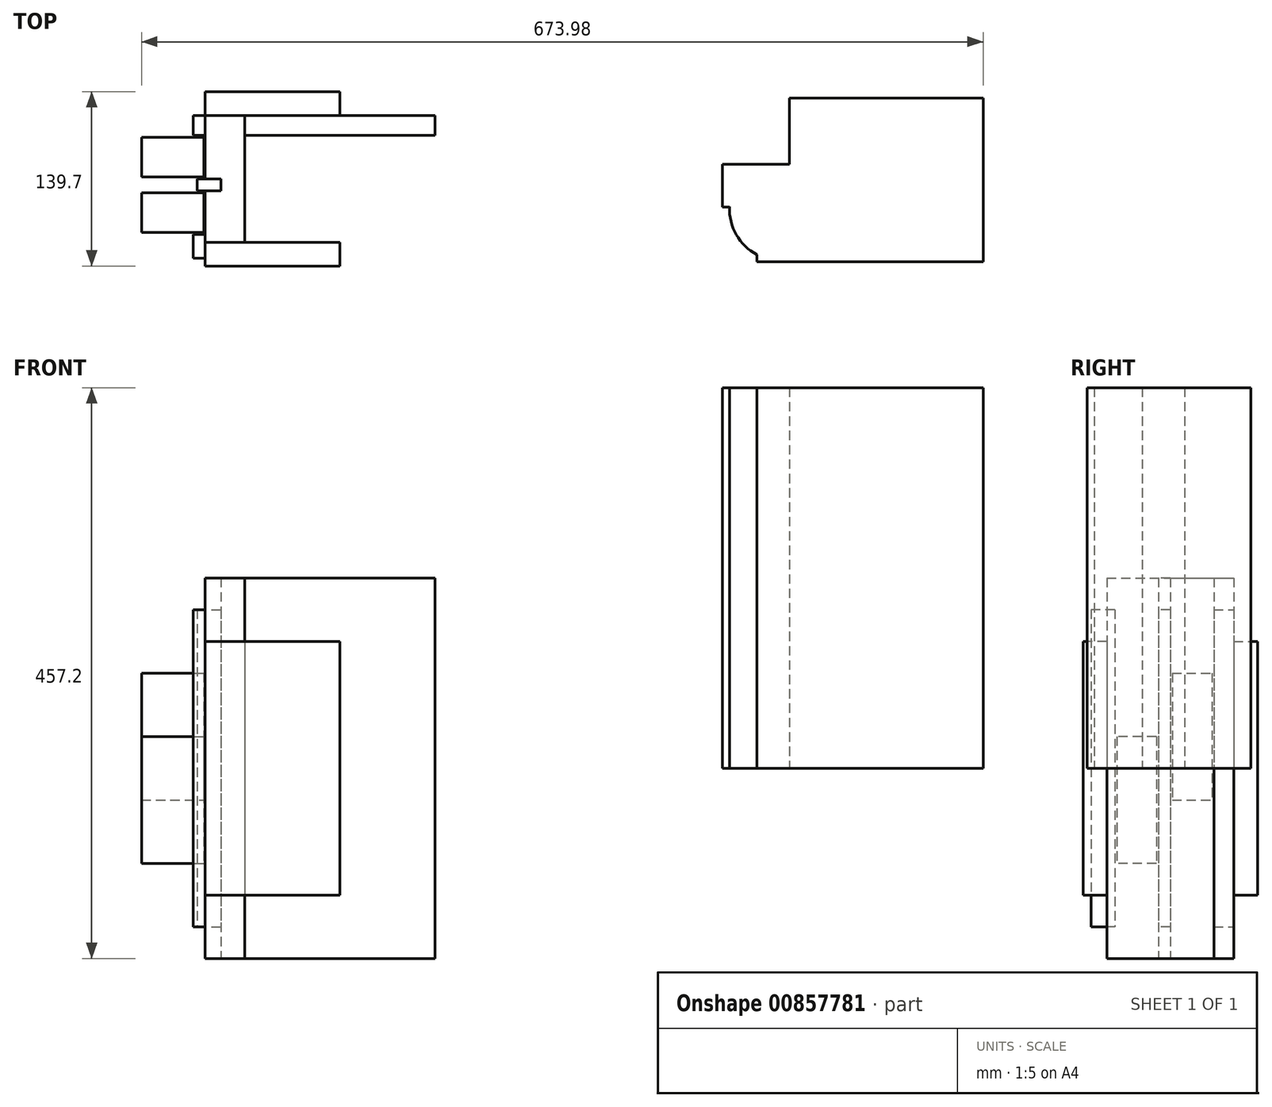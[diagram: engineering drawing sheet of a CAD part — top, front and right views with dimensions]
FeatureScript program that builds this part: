
annotation { "Feature Type Name" : "Feature", "Feature Type Description" : "" }
export const myFeature = defineFeature(function(context is Context, id is Id, definition is map)
    precondition{}
    {
        {
            var Q0;
            Q0=qCreatedBy(makeId("Top.planeOp"),FACE);
            var sketch = newSketch(context, id + "F0", { "sketchPlane" : qUnion([Q0])});
            skLineSegment(sketch, "E0.bottom", {"start": v(190.17, 63.13) * mm, "end": v(345.29, 63.13) * mm});
            skLineSegment(sketch, "E0.top", {"start": v(164.15, -68) * mm, "end": v(345.29, -68) * mm});
            skLineSegment(sketch, "E0.left", {"start": v(136.6, 10.06) * mm, "end": v(136.6, -24.12) * mm});
            skLineSegment(sketch, "E0.right", {"start": v(345.29, 63.13) * mm, "end": v(345.29, -68) * mm});
            skLineSegment(sketch, "E1.top", {"start": v(136.6, 10.06) * mm, "end": v(190.17, 10.06) * mm});
            skLineSegment(sketch, "E1.right", {"start": v(190.17, 63.13) * mm, "end": v(190.17, 10.06) * mm});
            skLineSegment(sketch, "E2.bottom", {"start": v(136.6, -24.12) * mm, "end": v(142.2, -24.12) * mm});
            skLineSegment(sketch, "E2.right", {"start": v(164.15, -62.4) * mm, "end": v(164.15, -68) * mm});
            skArc(sketch, "E3", {"start": v(142.2, -24.12) * mm, "mid": v(147.6, -46.46) * mm, "end": v(164.15, -62.4) * mm});
            skSolve(sketch);
        }
        {
            var Q0;
            Q0 = qSketchRegion(id + "F0", true);
            extrude(context, id + "F1", {"entities" : qUnion([Q0]), "depth" : 304.8 * mm, "offsetDistance" : 25.4 * mm});
        }
        {
            var Q0;
            Q0=qCreatedBy(makeId("Top.planeOp"),FACE);
            var sketch = newSketch(context, id + "F2", { "sketchPlane" : qUnion([Q0])});
            skLineSegment(sketch, "E4.bottom", {"start": v(-328.7, -12.7) * mm, "end": v(-278.69, -12.7) * mm});
            skLineSegment(sketch, "E4.top", {"start": v(-328.7, -44.45) * mm, "end": v(-278.69, -44.45) * mm});
            skLineSegment(sketch, "E4.left", {"start": v(-328.7, -12.7) * mm, "end": v(-328.7, -44.45) * mm});
            skLineSegment(sketch, "E4.right", {"start": v(-277.9, -12.7) * mm, "end": v(-277.9, -44.45) * mm});
            skLineSegment(sketch, "E5.bottom", {"start": v(-328.7, 0) * mm, "end": v(-278.69, 0) * mm});
            skLineSegment(sketch, "E5.top", {"start": v(-328.7, 31.75) * mm, "end": v(-278.69, 31.75) * mm});
            skLineSegment(sketch, "E5.left", {"start": v(-328.7, 0) * mm, "end": v(-328.7, 31.75) * mm});
            skLineSegment(sketch, "E5.right", {"start": v(-277.9, 0) * mm, "end": v(-277.9, 31.75) * mm});
            skLineSegment(sketch, "E6.bottom", {"start": v(-284.24, -1.59) * mm, "end": v(-265.2, -1.59) * mm});
            skLineSegment(sketch, "E6.top", {"start": v(-284.24, -11.11) * mm, "end": v(-265.2, -11.11) * mm});
            skLineSegment(sketch, "E6.left", {"start": v(-284.24, -1.59) * mm, "end": v(-284.24, -11.11) * mm});
            skLineSegment(sketch, "E6.right", {"start": v(-265.2, -1.59) * mm, "end": v(-265.2, -11.11) * mm});
            skLineSegment(sketch, "E7.bottom", {"start": v(-287.42, 33.34) * mm, "end": v(-277.9, 33.34) * mm});
            skLineSegment(sketch, "E7.top", {"start": v(-287.42, 49.21) * mm, "end": v(-277.9, 49.21) * mm});
            skLineSegment(sketch, "E7.left", {"start": v(-287.42, 33.34) * mm, "end": v(-287.42, 49.21) * mm});
            skLineSegment(sketch, "E7.right", {"start": v(-277.9, 33.34) * mm, "end": v(-277.9, 49.21) * mm});
            skLineSegment(sketch, "E8.bottom", {"start": v(-287.42, -46.04) * mm, "end": v(-277.9, -46.04) * mm});
            skLineSegment(sketch, "E8.top", {"start": v(-287.42, -65.09) * mm, "end": v(-277.9, -65.09) * mm});
            skLineSegment(sketch, "E8.left", {"start": v(-287.42, -46.04) * mm, "end": v(-287.42, -65.09) * mm});
            skLineSegment(sketch, "E8.right", {"start": v(-277.9, -46.04) * mm, "end": v(-277.9, -65.09) * mm});
            skLineSegment(sketch, "E9.top", {"start": v(-277.9, 49.21) * mm, "end": v(-246.14, 49.21) * mm});
            skLineSegment(sketch, "E9.left", {"start": v(-277.9, -71.44) * mm, "end": v(-277.9, -11.11) * mm});
            skLineSegment(sketch, "E9.right", {"start": v(-246.14, -52.39) * mm, "end": v(-246.14, 49.21) * mm});
            skLineSegment(sketch, "E10.bottom", {"start": v(-277.9, 49.21) * mm, "end": v(-169.94, 49.21) * mm});
            skLineSegment(sketch, "E10.top", {"start": v(-277.9, 68.26) * mm, "end": v(-169.94, 68.26) * mm});
            skLineSegment(sketch, "E10.left", {"start": v(-277.9, 49.21) * mm, "end": v(-277.9, 68.26) * mm});
            skLineSegment(sketch, "E10.right", {"start": v(-169.94, 49.21) * mm, "end": v(-169.94, 68.26) * mm});
            skLineSegment(sketch, "E11.bottom", {"start": v(-277.9, -52.39) * mm, "end": v(-169.94, -52.39) * mm});
            skLineSegment(sketch, "E11.top", {"start": v(-277.9, -71.44) * mm, "end": v(-169.94, -71.44) * mm});
            skLineSegment(sketch, "E11.left", {"start": v(-277.9, -52.39) * mm, "end": v(-277.9, -71.44) * mm});
            skLineSegment(sketch, "E11.right", {"start": v(-169.94, -52.39) * mm, "end": v(-169.94, -71.44) * mm});
            skLineSegment(sketch, "E12.trimOffspring", {"start": v(-277.9, -1.59) * mm, "end": v(-277.9, 49.21) * mm});
            skLineSegment(sketch, "E13", {"start": v(-278.69, 31.75) * mm, "end": v(-278.69, 0) * mm});
            skLineSegment(sketch, "E14", {"start": v(-278.69, -12.7) * mm, "end": v(-278.69, -44.45) * mm});
            skLineSegment(sketch, "E15.bottom", {"start": v(-246.14, 49.21) * mm, "end": v(-93.74, 49.21) * mm});
            skLineSegment(sketch, "E15.top", {"start": v(-246.14, 33.34) * mm, "end": v(-93.74, 33.34) * mm});
            skLineSegment(sketch, "E15.left", {"start": v(-246.14, 49.21) * mm, "end": v(-246.14, 33.34) * mm});
            skLineSegment(sketch, "E15.right", {"start": v(-93.74, 49.21) * mm, "end": v(-93.74, 33.34) * mm});
            skSolve(sketch);
        }
        {
            var Q0;
            Q0=makeQuery(id+"F2.imprint","IMPRINT",FACE,{"disambiguationData":[TD([[makeQuery(id+"F2.imprint","IMPRINT",EDGE,{"derivedFrom":sQuery(id+"F2.wireOp",EDGE,"E5.bottom")}),1.0]])]});
            extrude(context, id + "F3", {"entities" : qUnion([Q0]), "depth" : 76.2 * mm, "offsetDistance" : 25.4 * mm, "hasSecondDirection" : true, "secondDirectionOppositeDirection" : true, "secondDirectionDepth" : 25.4 * mm});
        }
        {
            var Q0;
            {var subQ0=sQuery(id+"F2.wireOp",EDGE,"E7.bottom");Q0=makeQuery(id+"F2.imprint","IMPRINT",FACE,{"disambiguationData":[TD([[makeQuery(id+"F2.imprint","IMPRINT",EDGE,{"derivedFrom":subQ0}),1.0]])]});}
            var Q1;
            {var subQ1=sQuery(id+"F2.wireOp",EDGE,"E8.bottom");Q1=makeQuery(id+"F2.imprint","IMPRINT",FACE,{"disambiguationData":[TD([[makeQuery(id+"F2.imprint","IMPRINT",EDGE,{"derivedFrom":subQ1}),-1.0]])]});}
            var Q2;
            {var subQ3=sQuery(id+"F2.wireOp",EDGE,"E6.left");Q2=makeQuery(id+"F2.imprint","IMPRINT",FACE,{"disambiguationData":[TD([[makeQuery(id+"F2.imprint","IMPRINT",EDGE,{"derivedFrom":subQ3}),1.0]])]});}
            extrude(context, id + "F4", {"entities" : qUnion([Q0, Q1, Q2]), "endBound" : BoundingType.SYMMETRIC, "depth" : 254 * mm, "offsetDistance" : 25.4 * mm});
        }
        {
            var Q0;
            Q0=makeQuery(id+"F2.imprint","IMPRINT",FACE,{"disambiguationData":[TD([[makeQuery(id+"F2.imprint","IMPRINT",EDGE,{"derivedFrom":sQuery(id+"F2.wireOp",EDGE,"E10.top")}),-1.0]])]});
            var Q1;
            {var subQ4=sQuery(id+"F2.wireOp",EDGE,"E11.top");Q1=makeQuery(id+"F2.imprint","IMPRINT",FACE,{"disambiguationData":[TD([[makeQuery(id+"F2.imprint","IMPRINT",EDGE,{"derivedFrom":subQ4}),1.0]])]});}
            extrude(context, id + "F5", {"entities" : qUnion([Q0, Q1]), "endBound" : BoundingType.SYMMETRIC, "depth" : 203.2 * mm, "offsetDistance" : 25.4 * mm});
        }
        {
            var Q0;
            {var subQ4=sQuery(id+"F2.wireOp",EDGE,"E6.right");Q0=makeQuery(id+"F2.imprint","IMPRINT",FACE,{"disambiguationData":[TD([[makeQuery(id+"F2.imprint","IMPRINT",EDGE,{"derivedFrom":subQ4}),1.0]])]});}
            extrude(context, id + "F6", {"entities" : qUnion([Q0]), "endBound" : BoundingType.SYMMETRIC, "depth" : 304.8 * mm, "offsetDistance" : 25.4 * mm});
        }
        {
            var Q0;
            Q0=makeQuery(id+"F2.imprint","IMPRINT",FACE,{"disambiguationData":[TD([[makeQuery(id+"F2.imprint","IMPRINT",EDGE,{"derivedFrom":sQuery(id+"F2.wireOp",EDGE,"E4.bottom")}),-1.0]])]});
            extrude(context, id + "F7", {"entities" : qUnion([Q0]), "depth" : 25.4 * mm, "offsetDistance" : 25.4 * mm, "hasSecondDirection" : true, "secondDirectionOppositeDirection" : true, "secondDirectionDepth" : 76.2 * mm});
        }
        {
            var Q0;
            Q0=makeQuery(id+"F2.imprint","IMPRINT",FACE,{"disambiguationData":[TD([[makeQuery(id+"F2.imprint","IMPRINT",EDGE,{"derivedFrom":sQuery(id+"F2.wireOp",EDGE,"E15.top")}),1.0]])]});
            extrude(context, id + "F8", {"entities" : qUnion([Q0]), "endBound" : BoundingType.SYMMETRIC, "depth" : 304.8 * mm, "offsetDistance" : 25.4 * mm});
        }
    });
